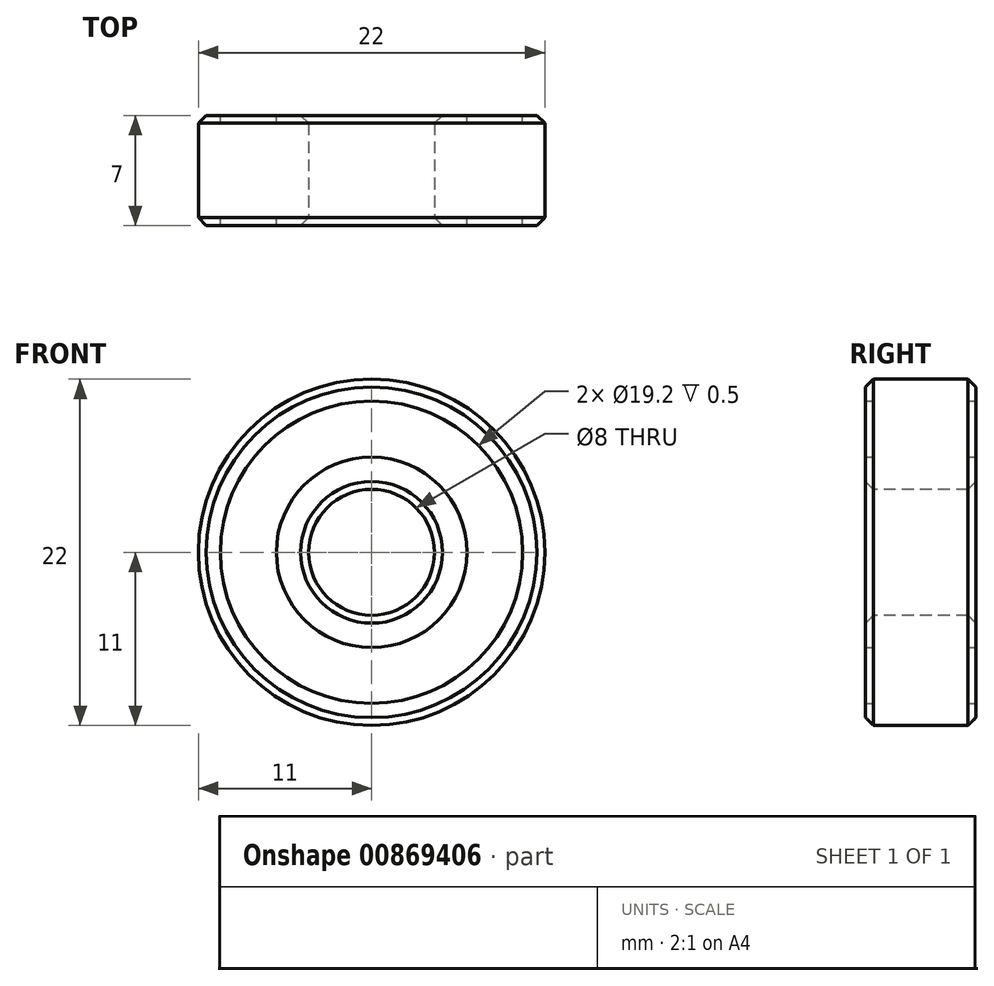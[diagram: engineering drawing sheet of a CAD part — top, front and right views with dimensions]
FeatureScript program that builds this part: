
annotation { "Feature Type Name" : "Feature", "Feature Type Description" : "" }
export const myFeature = defineFeature(function(context is Context, id is Id, definition is map)
    precondition{}
    {
        {
            var Q0;
            Q0=qCreatedBy(makeId("Front.planeOp"),FACE);
            var sketch = newSketch(context, id + "F0", { "sketchPlane" : qUnion([Q0])});
            skCircle(sketch, "E0", {"center": v(0, 0) * mm, "radius": 4 * mm});
            skCircle(sketch, "E1", {"center": v(0, 0) * mm, "radius": 11 * mm});
            skSolve(sketch);
        }
        {
            var Q0;
            Q0=makeQuery(id+"F0.imprint","IMPRINT",FACE,{"disambiguationData":[TD([[makeQuery(id+"F0.imprint","IMPRINT",EDGE,{"derivedFrom":sQuery(id+"F0.wireOp",EDGE,"E0")}),-1.0]])]});
            extrude(context, id + "F1", {"entities" : qUnion([Q0]), "oppositeDirection" : true, "depth" : 6 * mm, "offsetDistance" : 25 * mm});
        }
        {
            var Q0;
            Q0=makeQuery(id+"F1.opExtrude","CAP_FACE",FACE,{"disambiguationData":[OSD([sQuery(id+"F0.wireOp",EDGE,"E0"),sQuery(id+"F0.wireOp",EDGE,"E1")])],"isStart":true});
            var sketch = newSketch(context, id + "F2", { "sketchPlane" : qUnion([Q0])});
            skCircle(sketch, "E2", {"center": v(0, 0) * mm, "radius": 6.05 * mm});
            skCircle(sketch, "E3", {"center": v(0, 0) * mm, "radius": 9.6 * mm});
            skCircle(sketch, "E4.0", {"center": v(0, 0) * mm, "radius": 4 * mm});
            skCircle(sketch, "E5.0", {"center": v(0, 0) * mm, "radius": 11 * mm});
            skSolve(sketch);
        }
        {
            var Q0;
            Q0 = qSketchRegion(id + "F2", true);
            var Q1;
            Q1=makeQuery(id+"F2.imprint","IMPRINT",FACE,{"disambiguationData":[TD([[makeQuery(id+"F2.imprint","IMPRINT",EDGE,{"derivedFrom":sQuery(id+"F2.wireOp",EDGE,"E2")}),1.0]])]});
            extrude(context, id + "F3", {"entities" : qUnion([Q0, Q1]), "operationType" : NewBodyOperationType.ADD, "depth" : .5 * mm, "offsetDistance" : 25 * mm, "hasSecondDirection" : true, "secondDirectionOppositeDirection" : true, "secondDirectionDepth" : 6.5 * mm});
        }
        {
            var Q0;
            Q0=makeQuery(id+"F3.opExtrude","CAP_EDGE",EDGE,{"disambiguationData":[OSD([sQuery(id+"F2.wireOp",EDGE,"E5.0")])],"isStart":false});
            var Q1;
            Q1=makeQuery(id+"F3.opExtrude","CAP_EDGE",EDGE,{"disambiguationData":[OSD([sQuery(id+"F2.wireOp",EDGE,"E4.0")])],"isStart":false});
            var Q2;
            Q2=makeQuery(id+"F3.opExtrude","CAP_EDGE",EDGE,{"disambiguationData":[OSD([sQuery(id+"F2.wireOp",EDGE,"E5.0")])],"isStart":true});
            var Q3;
            Q3=makeQuery(id+"F3.opExtrude","CAP_EDGE",EDGE,{"disambiguationData":[OSD([sQuery(id+"F2.wireOp",EDGE,"E4.0")])],"isStart":true});
            chamfer(context, id + "F4", {"entities" : qUnion([Q0, Q1, Q2, Q3]), "width" : .5 * mm, "tangentPropagation" : true});
        }
    });
